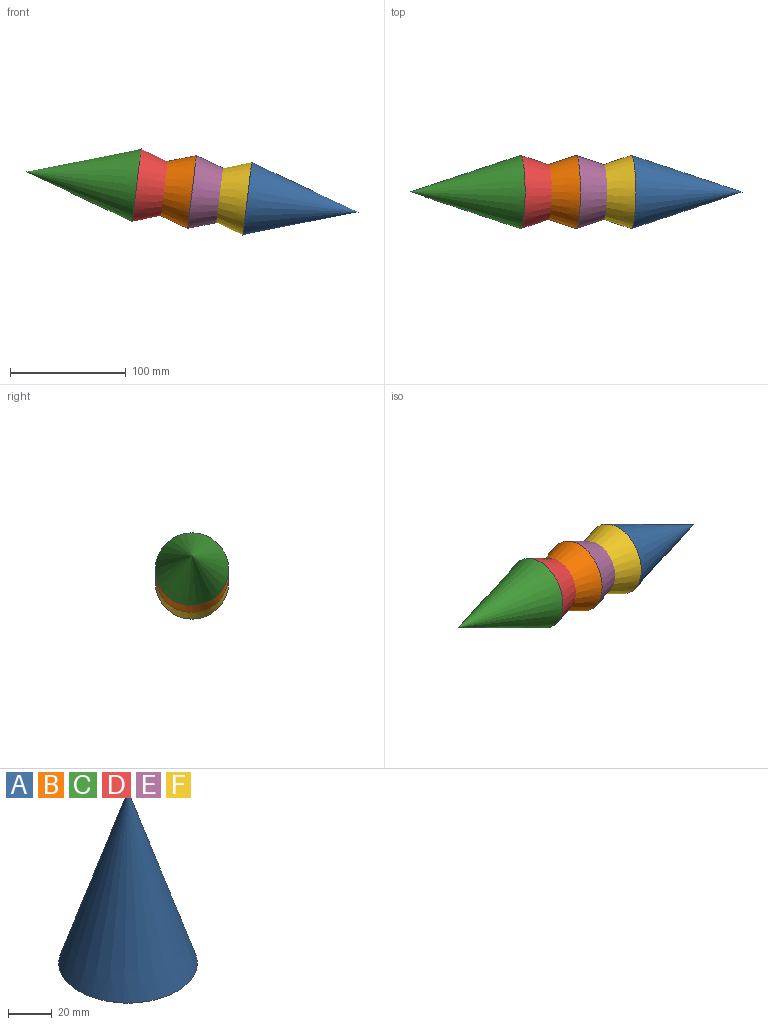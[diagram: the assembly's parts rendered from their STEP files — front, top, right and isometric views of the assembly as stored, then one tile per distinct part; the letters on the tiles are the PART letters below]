
ASSEMBLY  parts=6 mates=5
PART A: 2 faces, bbox 63.5x63.5x96.5 mm
  f0: cone r=0mm half-angle=18.2deg, axis (0,0,-1), area 10134.1mm2, adj f1
  f1: plane 63.5x63.5mm, normal (0,0,-1), area 3166.9mm2, adj f0
PART B: same geometry as A
PART C: same geometry as A
PART D: same geometry as A
PART E: same geometry as A
PART F: same geometry as A
PLACE A rot(axis=(-0.6,0.6,-0.53),124.1deg) t=(41.54,53.63,-106.78)mm
PLACE B rot(axis=(0,-1,0),83.1deg) t=(-124.75,53.63,-86.63)mm
PLACE C rot(axis=(0.55,-0.55,-0.62),116.1deg) t=(-172.66,53.63,-80.82)mm
PLACE D rot(axis=(0.6,0.6,0.53),124.1deg) t=(-54.27,53.63,-95.17)mm
PLACE E rot(axis=(0,1,0),96.9deg) t=(-6.37,53.63,-100.98)mm
PLACE F rot(axis=(0.55,-0.55,-0.62),116.1deg) t=(-76.85,53.63,-92.43)mm
MATE fastened F.f0 <-> A.f0  axis (0.99,0,-0.12) through (-17.66,53.63,-99.61)mm
MATE fastened B.f0 <-> E.f0  axis (0.99,0,-0.12) through (-65.56,53.63,-93.8)mm
MATE fastened F.f0 <-> E.f0  axis (0.99,0,-0.12) through (-65.56,53.63,-93.8)mm
MATE fastened D.f0 <-> C.f0  axis (-0.99,0,0.12) through (-113.47,53.63,-87.99)mm
MATE fastened C.f0 <-> F.f0  axis (0.99,0,-0.12) through (-113.47,53.63,-87.99)mm
